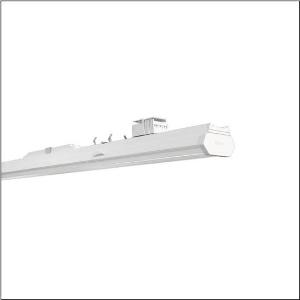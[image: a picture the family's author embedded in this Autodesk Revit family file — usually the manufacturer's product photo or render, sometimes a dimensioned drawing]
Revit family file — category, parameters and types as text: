
# Revit family: licross_r__21_protected_ho_52td12dn4axm_e376
name_source: partatom
category: Lighting Fixtures
units: mm (PartAtom-declared; Revit-internal decimal feet)

## family parameters
Cut with Voids When Loaded = No
Host = Face
Light Source = No
Part Type = Normal
Room Calculation Point = No
Round Connector Dimension = Use Diameter
Shared = No

## types (1)
- --- (1 x LED, 10000 lm, 56 W, 4000K)
    Apparent Load = 56 VA
    CIE Flux Codes = 70 91 97 98 100
    Color Rendering = 80
    Color Temperature = 4000K
    Default Elevation = 1800 mm
    Description = Licross® 21 Protected HO, luminaire insert, of sheet steel, galvanised, coil coated, white, length: 1.500mm, width: 90mm, height: 103mm, LED rated luminous flux: 10.000lm, light colour: 840, SDCM (Standard Deviation of Colour Matching)MacAdam ≤ 3 SDCM (initial), control gear: DALI 2, with plug, 5-pole, with phase selection, mains connection: 220..240V, AC, 50/60Hz, rated input power: 56W, internal wiring halogen-free, primary light control with lens, of plastic, primary optical cover: cover, of PMMA, light emission: direct distribution, primary light characteristic: symmetric, protection rating (complete): IP54, insulation class (complete): insulation class I (protective earthing), certification: CE, ENEC, VDE, UKCA, protection symbol: D if used in an environment with non-conductive dust loads with corresponding accessories, impact resistance: IK06, permissible ambient temperature for indoor applications: -25..+45°C, corresponds to IFS (International Featured Standards) requirements for safety and quality in the food industry, reducing of maximum allowable ambient temperature of 5°C with ceiling mounting, LABS conformity tested according to VDMA 24364:2018-05, packaging unit: 1 piece
    Height = 92 mm
    Lamp = 1 x LED
    Lamp Light Flux = 10000 lm
    Lamp Power = 56 W
    Lamp count = 1
    Length = 1500 mm
    Luminous efficacy = 179 lm/W
    Manufacturer = Siteco
    ModVariant = No
    Model = 52TD12DN4AXM
    Mounting Place = Ceiling
    Mounting Type = Pendant
    Number of Poles = 1
    OnlyDefault = Yes
    Power Factor = 1
    Product Name = Licross® 21 Protected HO
    Product group = luminaire insert | ceiling pendant
    ProductGroupID = 901
    Protection Class = Protection class I
    Protection Degree = IP 54
    RLX_Detail_Level = 1
    RLX_Emergency_Light_Flux = 0 lm
    RLX_Emergency_Type = 0
    RLX_Emergency_Type_DB = No
    RlxData = <blob elided: 24245 chars, md5=ea17bc3a>
    Socket = socket
    Standby Power = 0 W
    System Light Flux = 10000 lm
    System Power = 56 W
    Type Comments = factory setting: luminous flux: 100 % | dim-lin: 254 | 321 mA
    Type Image = l_1256148.jpg
    URL = http://relux.com
    VarID = @adj_132919
    Voltage = 0 V
    Weight = 0.00 kg
    Width = 88 mm

## geometry (parser evidence)
native form markers: Blend x4, Sweep x10
no freeform markers — native parametric forms only
